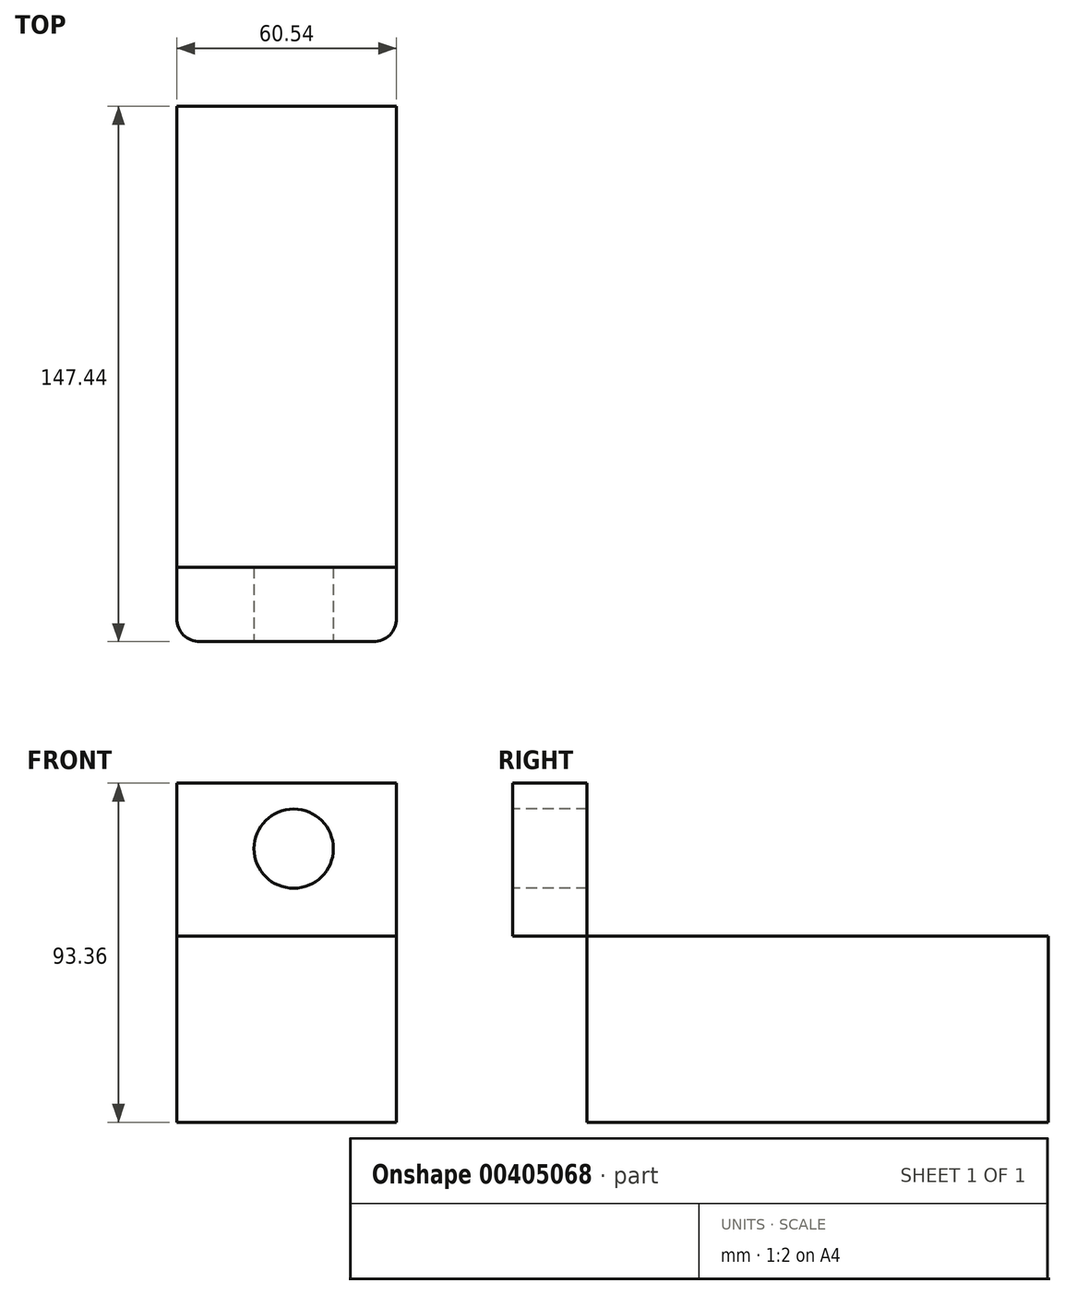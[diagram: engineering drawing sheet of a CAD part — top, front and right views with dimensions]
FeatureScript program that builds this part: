
annotation { "Feature Type Name" : "Feature", "Feature Type Description" : "" }
export const myFeature = defineFeature(function(context is Context, id is Id, definition is map)
    precondition{}
    {
        {
            var Q0;
            Q0=qCreatedBy(makeId("Front.planeOp"),FACE);
            var sketch = newSketch(context, id + "F0", { "sketchPlane" : qUnion([Q0])});
            skLineSegment(sketch, "E0.bottom", {"start": v(-30.27, 25.6) * mm, "end": v(30.27, 25.6) * mm});
            skLineSegment(sketch, "E0.top", {"start": v(-30.27, -25.6) * mm, "end": v(30.27, -25.6) * mm});
            skLineSegment(sketch, "E0.left", {"start": v(-30.27, 25.6) * mm, "end": v(-30.27, -25.6) * mm});
            skLineSegment(sketch, "E0.right", {"start": v(30.27, 25.6) * mm, "end": v(30.27, -25.6) * mm});
            skPoint(sketch, "E0.middle", {"position": v(0, 0) * mm});
            skSolve(sketch);
        }
        {
            var Q0;
            Q0=makeQuery(id+"F0.imprint","IMPRINT",FACE,{"disambiguationData":[TD([[makeQuery(id+"F0.imprint","IMPRINT",EDGE,{"derivedFrom":sQuery(id+"F0.wireOp",EDGE,"E0.bottom")}),-1.0]])]});
            extrude(context, id + "F1", {"entities" : qUnion([Q0]), "depth" : 127 * mm});
        }
        {
            var Q0;
            Q0=makeQuery(id+"F1.opExtrude","SWEPT_FACE",FACE,{"disambiguationData":[OSD([sQuery(id+"F0.wireOp",EDGE,"E0.bottom")])]});
            var sketch = newSketch(context, id + "F2", { "sketchPlane" : qUnion([Q0])});
            skLineSegment(sketch, "E1", {"start": v(-30.27, -127) * mm, "end": v(-30.27, -141.09) * mm});
            skLineSegment(sketch, "E2", {"start": v(-23.92, -147.44) * mm, "end": v(23.92, -147.44) * mm});
            skLineSegment(sketch, "E3", {"start": v(30.27, -141.09) * mm, "end": v(30.27, -127) * mm});
            skPoint(sketch, "E4.visualSharp", {"position": v(-30.27, -147.44) * mm});
            skArc(sketch, "E4.filletArc", {"start": v(-30.27, -141.09) * mm, "mid": v(-28.4, -145.58) * mm, "end": v(-23.92, -147.44) * mm});
            skPoint(sketch, "E5.visualSharp", {"position": v(30.27, -147.44) * mm});
            skArc(sketch, "E5.filletArc", {"start": v(23.92, -147.44) * mm, "mid": v(28.4, -145.58) * mm, "end": v(30.27, -141.09) * mm});
            skSolve(sketch);
        }
        {
            var Q0;
            Q0=makeQuery(id+"F2.imprint","IMPRINT",FACE,{"disambiguationData":[TD([[makeQuery(id+"F2.imprint","IMPRINT",EDGE,{"derivedFrom":sQuery(id+"F2.wireOp",EDGE,"E1")}),1.0]])]});
            extrude(context, id + "F3", {"entities" : qUnion([Q0]), "depth" : 42.16 * mm});
        }
        {
            var Q0;
            Q0=makeQuery(id+"F3.opExtrude","SWEPT_FACE",FACE,{"disambiguationData":[OSD([sQuery(id+"F2.wireOp",EDGE,"E2")])]});
            var sketch = newSketch(context, id + "F4", { "sketchPlane" : qUnion([Q0])});
            skCircle(sketch, "E6", {"center": v(1.95, 49.76) * mm, "radius": 10.92 * mm});
            skSolve(sketch);
        }
        {
            var Q0;
            Q0=makeQuery(id+"F4.imprint","IMPRINT",FACE,{"disambiguationData":[TD([[makeQuery(id+"F4.imprint","IMPRINT",EDGE,{"derivedFrom":sQuery(id+"F4.wireOp",EDGE,"E6")}),1.0]])]});
            extrude(context, id + "F5", {"entities" : qUnion([Q0]), "operationType" : NewBodyOperationType.REMOVE, "oppositeDirection" : true, "depth" : 25.4 * mm});
        }
        {
            var Q0;
            Q0=makeQuery(id+"F1.opExtrude","SWEPT_FACE",FACE,{"disambiguationData":[OSD([sQuery(id+"F0.wireOp",EDGE,"E0.right")])]});
            var sketch = newSketch(context, id + "F6", { "sketchPlane" : qUnion([Q0])});
            skArc(sketch, "E7", {"start": v(-61.12, 0) * mm, "mid": v(-75.87, 13.22) * mm, "end": v(-90.61, 0) * mm});
            skSolve(sketch);
        }
        {
            var Q0;
            Q0=sQuery(id+"F6.wireOp",EDGE,"E7");
            var Q1;
            Q1=makeQuery(id+"F3.opExtrude","CAP_EDGE",EDGE,{"disambiguationData":[OSD([sQuery(id+"F2.wireOp",EDGE,"E3")])],"isStart":false});
            revolve(context, id + "F7", {"bodyType" : ToolBodyType.SURFACE, "surfaceEntities" : qUnion([Q0]), "axis" : qUnion([Q1]), "revolveType" : RevolveType.FULL});
        }
    });
